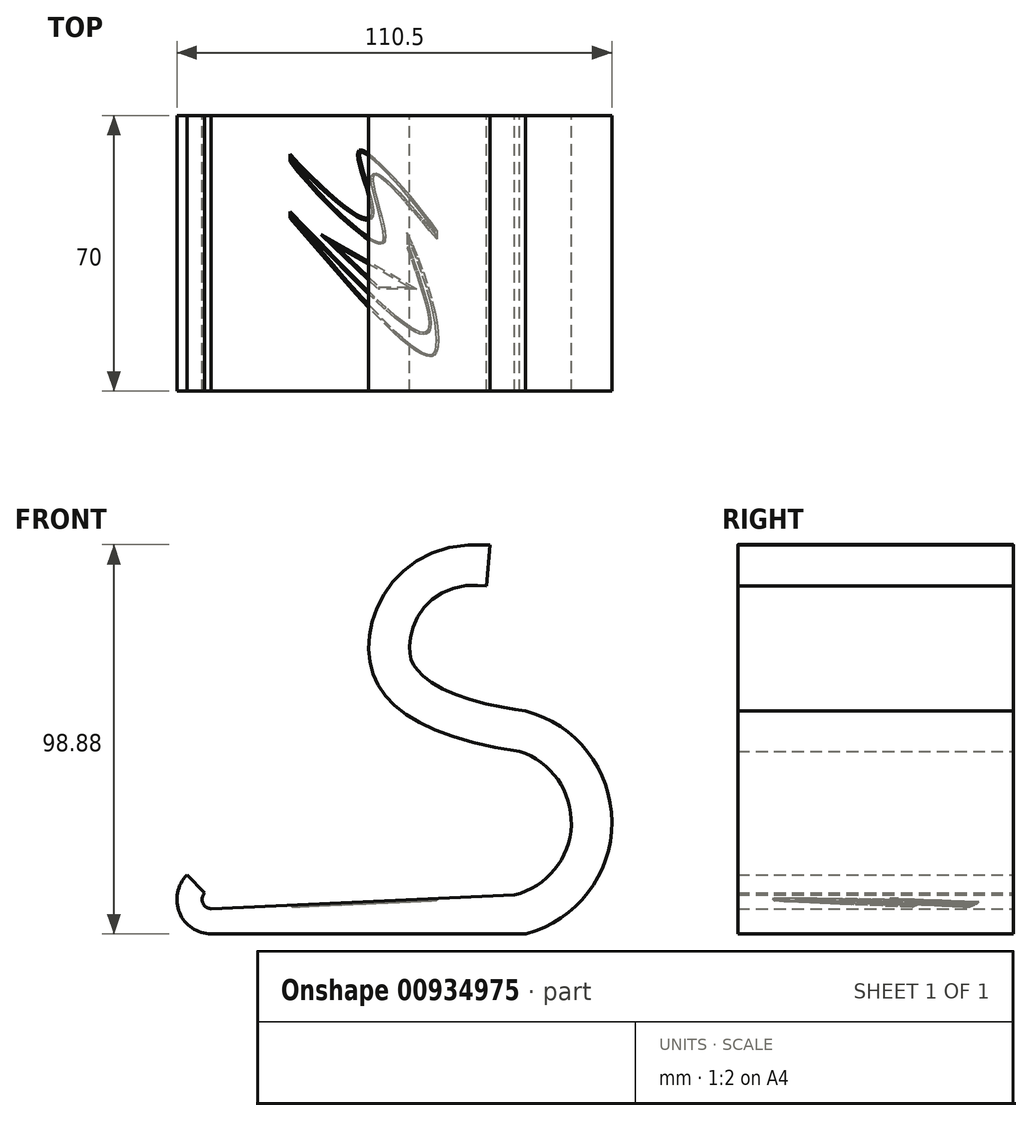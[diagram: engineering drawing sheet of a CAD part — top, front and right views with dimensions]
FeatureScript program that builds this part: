
annotation { "Feature Type Name" : "Feature", "Feature Type Description" : "" }
export const myFeature = defineFeature(function(context is Context, id is Id, definition is map)
    precondition{}
    {
        {
            var Q0;
            Q0=qCreatedBy(makeId("Front.planeOp"),FACE);
            var sketch = newSketch(context, id + "F0", { "sketchPlane" : qUnion([Q0])});
            skLineSegment(sketch, "E0", {"start": v(0, 0) * mm, "end": v(0, 100) * mm, "construction": true});
            skLineSegment(sketch, "E1", {"start": v(0, 0) * mm, "end": v(-40, 0) * mm});
            skLineSegment(sketch, "E2", {"start": v(0, 0) * mm, "end": v(40, 0) * mm});
            skArc(sketch, "E3", {"start": v(-46.17, 14.93) * mm, "mid": v(-48.08, 5.4) * mm, "end": v(-40, 0) * mm});
            skArc(sketch, "E4.2", {"start": v(37.04, 9.88) * mm, "mid": v(51.45, 27.63) * mm, "end": v(38.33, 46.36) * mm});
            skArc(sketch, "E5.0", {"start": v(-41.65, 10.4) * mm, "mid": v(-42.16, 7.85) * mm, "end": v(-40, 6.4) * mm});
            skLineSegment(sketch, "E6", {"start": v(37.04, 9.88) * mm, "end": v(-40, 6.4) * mm});
            skLineSegment(sketch, "E7", {"start": v(-41.65, 10.4) * mm, "end": v(-46.17, 14.93) * mm});
            skFitSpline(sketch, "E8", {"points": [v(38.33, 46.36) * mm, v(0, 71.82) * mm, v(30.83, 98.74) * mm], "startDerivative": vector(-149.61, 21.91) * mm, "endDerivative": vector(132.7, -11.42) * mm});
            skFitSpline(sketch, "E9.0", {"points": [v(39.83, 56.65) * mm, v(36.93, 57.08) * mm, v(31.58, 58.05) * mm, v(24.9, 59.83) * mm, v(19.6, 61.84) * mm, v(15.7, 63.97) * mm, v(13.54, 65.69) * mm, v(12.36, 66.96) * mm, v(11.7, 67.86) * mm, v(11.2, 68.72) * mm, v(10.84, 69.6) * mm, v(10.57, 70.56) * mm, v(10.4, 71.63) * mm, v(10.36, 72.9) * mm, v(10.49, 74.79) * mm, v(11.05, 77.38) * mm, v(12.41, 80.49) * mm, v(14.4, 83.28) * mm, v(16.96, 85.58) * mm, v(20.16, 87.34) * mm, v(24.28, 88.44) * mm, v(27.89, 88.55) * mm, v(29.94, 88.38) * mm]});
            skLineSegment(sketch, "E10", {"start": v(29.94, 88.38) * mm, "end": v(30.83, 98.74) * mm});
            skArc(sketch, "E11.0", {"start": v(40, 0) * mm, "mid": v(61.76, 28.4) * mm, "end": v(39.8, 56.66) * mm});
            skSolve(sketch);
        }
        {
            var Q0;
            Q0=makeQuery(id+"F0.imprint","IMPRINT",FACE,{"disambiguationData":[TD([[makeQuery(id+"F0.imprint","IMPRINT",EDGE,{"derivedFrom":sQuery(id+"F0.wireOp",EDGE,"E1")}),-1.0]])]});
            extrude(context, id + "F1", {"entities" : qUnion([Q0]), "depth" : 35 * mm, "offsetDistance" : 25 * mm, "hasSecondDirection" : true, "secondDirectionOppositeDirection" : true, "secondDirectionDepth" : 35 * mm});
        }
        {
            var Q0;
            Q0=makeQuery(id+"F1.opExtrude","SWEPT_FACE",FACE,{"disambiguationData":[OSD([sQuery(id+"F0.wireOp",EDGE,"E6")])]});
            var sketch = newSketch(context, id + "F2", { "sketchPlane" : qUnion([Q0])});
            skPoint(sketch, "E12.positionSnap0", {"position": v(-39.67, 0) * mm});
            skPoint(sketch, "E12.positionSnap1", {"position": v(-1.11, 35) * mm});
            skLineSegment(sketch, "E13", {"start": v(-19.66, 10.69) * mm, "end": v(-19.66, 8.95) * mm});
            skLineSegment(sketch, "E14", {"start": v(-19.66, 25.24) * mm, "end": v(-19.66, 23.32) * mm});
            skLineSegment(sketch, "E15.MirrorCS", {"start": v(-1.77, 26.28) * mm, "end": v(-2.06, 26.21) * mm});
            skLineSegment(sketch, "E16.MirrorCS", {"start": v(1.54, 19.5) * mm, "end": v(1.46, 19.02) * mm});
            skLineSegment(sketch, "E17.MirrorCS", {"start": v(1.77, 19.78) * mm, "end": v(1.54, 19.5) * mm});
            skLineSegment(sketch, "E18.MirrorCS", {"start": v(1.46, 19.02) * mm, "end": v(1.48, 18.36) * mm});
            skLineSegment(sketch, "E19.MirrorCS", {"start": v(-2.06, 26.21) * mm, "end": v(-2.27, 26.01) * mm});
            skLineSegment(sketch, "E20.MirrorCS", {"start": v(-2.4, 25.63) * mm, "end": v(-2.44, 25.1) * mm});
            skLineSegment(sketch, "E21.MirrorCS", {"start": v(-2.27, 26.01) * mm, "end": v(-2.4, 25.63) * mm});
            skLineSegment(sketch, "E22.MirrorCS", {"start": v(-1.4, 26.23) * mm, "end": v(-1.77, 26.28) * mm});
            skLineSegment(sketch, "E23.MirrorCS", {"start": v(1.07, 10.9) * mm, "end": v(1.08, 10.23) * mm});
            skLineSegment(sketch, "E24.MirrorCS", {"start": v(1.08, 10.23) * mm, "end": v(0.99, 9.69) * mm});
            skLineSegment(sketch, "E25.MirrorCS", {"start": v(-2.45, 9.75) * mm, "end": v(-4.03, 10.74) * mm});
            skLineSegment(sketch, "E26.MirrorCS", {"start": v(12.35, -24.75) * mm, "end": v(10.73, -23.6) * mm});
            skLineSegment(sketch, "E27.MirrorCS", {"start": v(1.96, 24) * mm, "end": v(0.86, 24.9) * mm});
            skLineSegment(sketch, "E28.MirrorCS", {"start": v(4.57, 3.56) * mm, "end": v(4.45, 3.08) * mm});
            skLineSegment(sketch, "E29.MirrorCS", {"start": v(14.83, -20.03) * mm, "end": v(14.33, -20.12) * mm});
            skLineSegment(sketch, "E30.MirrorCS", {"start": v(18.11, -22) * mm, "end": v(18, -23.76) * mm});
            skLineSegment(sketch, "E31.MirrorCS", {"start": v(-0.37, 8.93) * mm, "end": v(-1.32, 9.2) * mm});
            skLineSegment(sketch, "E32.MirrorCS", {"start": v(2.14, 19.84) * mm, "end": v(1.77, 19.78) * mm});
            skLineSegment(sketch, "E33.MirrorCS", {"start": v(15.84, -26.22) * mm, "end": v(15.06, -26.1) * mm});
            skLineSegment(sketch, "E34.MirrorCS", {"start": v(3.46, 2.33) * mm, "end": v(2.81, 2.39) * mm});
            skLineSegment(sketch, "E35.MirrorCS", {"start": v(0.99, 9.69) * mm, "end": v(0.64, 9.12) * mm});
            skLineSegment(sketch, "E36.MirrorCS", {"start": v(15.68, -17.7) * mm, "end": v(15.62, -18.72) * mm});
            skLineSegment(sketch, "E37.MirrorCS", {"start": v(-0.11, 25.6) * mm, "end": v(-0.94, 26.07) * mm});
            skLineSegment(sketch, "E38.MirrorCS", {"start": v(17.05, -25.85) * mm, "end": v(16.5, -26.14) * mm});
            skLineSegment(sketch, "E39.MirrorCS", {"start": v(6.33, 16.67) * mm, "end": v(4.91, 18.02) * mm});
            skLineSegment(sketch, "E40.MirrorCS", {"start": v(4.91, 18.02) * mm, "end": v(3.69, 19.04) * mm});
            skLineSegment(sketch, "E41.MirrorCS", {"start": v(2.03, 15.55) * mm, "end": v(2.46, 13.92) * mm});
            skLineSegment(sketch, "E42.MirrorCS", {"start": v(-1.32, 9.2) * mm, "end": v(-2.45, 9.75) * mm});
            skLineSegment(sketch, "E43.MirrorCS", {"start": v(15.47, -19.32) * mm, "end": v(15.2, -19.76) * mm});
            skLineSegment(sketch, "E44.MirrorCS", {"start": v(14.33, -20.12) * mm, "end": v(13.45, -19.98) * mm});
            skLineSegment(sketch, "E45.MirrorCS", {"start": v(2.82, 19.6) * mm, "end": v(2.14, 19.84) * mm});
            skLineSegment(sketch, "E46.MirrorCS", {"start": v(3.69, 19.04) * mm, "end": v(2.82, 19.6) * mm});
            skLineSegment(sketch, "E47.MirrorCS", {"start": v(11.07, -18.77) * mm, "end": v(9.33, -17.55) * mm});
            skLineSegment(sketch, "E48.MirrorCS", {"start": v(15.2, -19.76) * mm, "end": v(14.83, -20.03) * mm});
            skLineSegment(sketch, "E49.MirrorCS", {"start": v(0.78, 3.26) * mm, "end": v(-0.67, 4.19) * mm});
            skLineSegment(sketch, "E50.MirrorCS", {"start": v(13.45, -19.98) * mm, "end": v(12.36, -19.52) * mm});
            skLineSegment(sketch, "E51.MirrorCS", {"start": v(17.48, -25.35) * mm, "end": v(17.05, -25.85) * mm});
            skLineSegment(sketch, "E52.MirrorCS", {"start": v(0.2, 8.93) * mm, "end": v(-0.37, 8.93) * mm});
            skLineSegment(sketch, "E53.MirrorCS", {"start": v(15.33, -14.96) * mm, "end": v(15.58, -16.43) * mm});
            skLineSegment(sketch, "E54.MirrorCS", {"start": v(0.86, 24.9) * mm, "end": v(-0.11, 25.6) * mm});
            skLineSegment(sketch, "E55.MirrorCS", {"start": v(18, -23.76) * mm, "end": v(17.8, -24.64) * mm});
            skLineSegment(sketch, "E56.MirrorCS", {"start": v(13.8, -25.6) * mm, "end": v(12.35, -24.75) * mm});
            skLineSegment(sketch, "E57.MirrorCS", {"start": v(0.86, 12.4) * mm, "end": v(1.07, 10.9) * mm});
            skLineSegment(sketch, "E58.MirrorCS", {"start": v(2.05, 2.63) * mm, "end": v(0.78, 3.26) * mm});
            skLineSegment(sketch, "E59.MirrorCS", {"start": v(4.45, 3.08) * mm, "end": v(4.25, 2.71) * mm});
            skLineSegment(sketch, "E60.MirrorCS", {"start": v(1.48, 18.36) * mm, "end": v(1.7, 17) * mm});
            skLineSegment(sketch, "E61.MirrorCS", {"start": v(3.96, 2.47) * mm, "end": v(3.46, 2.33) * mm});
            skLineSegment(sketch, "E62.MirrorCS", {"start": v(15.06, -26.1) * mm, "end": v(13.8, -25.6) * mm});
            skLineSegment(sketch, "E63.MirrorCS", {"start": v(4.25, 2.71) * mm, "end": v(3.96, 2.47) * mm});
            skLineSegment(sketch, "E64.MirrorCS", {"start": v(4.62, 4.15) * mm, "end": v(4.57, 3.56) * mm});
            skLineSegment(sketch, "E65.MirrorCS", {"start": v(0.64, 9.12) * mm, "end": v(0.2, 8.93) * mm});
            skLineSegment(sketch, "E66.MirrorCS", {"start": v(4.5, 5.71) * mm, "end": v(4.62, 4.15) * mm});
            skLineSegment(sketch, "E67.MirrorCS", {"start": v(1.7, 17) * mm, "end": v(2.03, 15.55) * mm});
            skLineSegment(sketch, "E68.MirrorCS", {"start": v(15.58, -16.43) * mm, "end": v(15.68, -17.7) * mm});
            skLineSegment(sketch, "E69.MirrorCS", {"start": v(12.36, -19.52) * mm, "end": v(11.07, -18.77) * mm});
            skLineSegment(sketch, "E70.MirrorCS", {"start": v(15.62, -18.72) * mm, "end": v(15.47, -19.32) * mm});
            skLineSegment(sketch, "E71.MirrorCS", {"start": v(-2.44, 25.1) * mm, "end": v(-2.32, 24.01) * mm});
            skLineSegment(sketch, "E72.MirrorCS", {"start": v(2.81, 2.39) * mm, "end": v(2.05, 2.63) * mm});
            skLineSegment(sketch, "E73.MirrorCS", {"start": v(16.5, -26.14) * mm, "end": v(15.84, -26.22) * mm});
            skLineSegment(sketch, "E74.MirrorCS", {"start": v(17.8, -24.64) * mm, "end": v(17.48, -25.35) * mm});
            skLineSegment(sketch, "E75.MirrorCS", {"start": v(-0.94, 26.07) * mm, "end": v(-1.4, 26.23) * mm});
            skLineSegment(sketch, "E76.MirrorCS", {"start": v(-4.01, 6.8) * mm, "end": v(-6.92, 9.42) * mm});
            skLineSegment(sketch, "E77.MirrorCS", {"start": v(6.92, 19.12) * mm, "end": v(5.17, 20.95) * mm});
            skLineSegment(sketch, "E78.MirrorCS", {"start": v(-2.28, 5.38) * mm, "end": v(-4.01, 6.8) * mm});
            skLineSegment(sketch, "E79.MirrorCS", {"start": v(-17.56, 20.72) * mm, "end": v(-19.66, 23.32) * mm});
            skLineSegment(sketch, "E80.MirrorCS", {"start": v(16.5, -12.1) * mm, "end": v(17.17, -14.89) * mm});
            skLineSegment(sketch, "E81.MirrorCS", {"start": v(15.85, 5.86) * mm, "end": v(13.81, 8.3) * mm});
            skLineSegment(sketch, "E82.MirrorCS", {"start": v(-7.7, 13.6) * mm, "end": v(-9.72, 15.35) * mm});
            skLineSegment(sketch, "E83.MirrorCS", {"start": v(12.92, 12.2) * mm, "end": v(10.98, 14.55) * mm});
            skLineSegment(sketch, "E84.MirrorCS", {"start": v(4.75, -13.73) * mm, "end": v(1.89, -11.1) * mm});
            skLineSegment(sketch, "E85.MirrorCS", {"start": v(9.33, -17.55) * mm, "end": v(7.36, -15.98) * mm});
            skLineSegment(sketch, "E86.MirrorCS", {"start": v(3.63, 9.66) * mm, "end": v(4.14, 7.59) * mm});
            skLineSegment(sketch, "E87.MirrorCS", {"start": v(4.14, 7.59) * mm, "end": v(4.5, 5.71) * mm});
            skLineSegment(sketch, "E88.MirrorCS", {"start": v(8.62, -21.86) * mm, "end": v(6.34, -19.78) * mm});
            skLineSegment(sketch, "E89.MirrorCS", {"start": v(-9.78, -2.45) * mm, "end": v(-13.21, 1.5) * mm});
            skLineSegment(sketch, "E90.MirrorCS", {"start": v(-0.12, 16.19) * mm, "end": v(0.46, 14.14) * mm});
            skLineSegment(sketch, "E91.MirrorCS", {"start": v(7.87, 15.07) * mm, "end": v(6.33, 16.67) * mm});
            skLineSegment(sketch, "E92.MirrorCS", {"start": v(11.67, 10.82) * mm, "end": v(9.52, 13.27) * mm});
            skLineSegment(sketch, "E93.MirrorCS", {"start": v(-15.17, 17.96) * mm, "end": v(-17.56, 20.72) * mm});
            skLineSegment(sketch, "E94.MirrorCS", {"start": v(0.36, -13.74) * mm, "end": v(-2.82, -10.3) * mm});
            skLineSegment(sketch, "E95.MirrorCS", {"start": v(2.46, 13.92) * mm, "end": v(3.05, 11.8) * mm});
            skLineSegment(sketch, "E96.MirrorCS", {"start": v(7.36, -15.98) * mm, "end": v(4.75, -13.73) * mm});
            skLineSegment(sketch, "E97.MirrorCS", {"start": v(-4.03, 10.74) * mm, "end": v(-5.8, 12.04) * mm});
            skLineSegment(sketch, "E98.MirrorCS", {"start": v(3.05, 11.8) * mm, "end": v(3.63, 9.66) * mm});
            skLineSegment(sketch, "E99.MirrorCS", {"start": v(-1.95, 22.34) * mm, "end": v(-1.4, 20.4) * mm});
            skLineSegment(sketch, "E100.MirrorCS", {"start": v(12.47, -9) * mm, "end": v(2.77, -9) * mm});
            skLineSegment(sketch, "E101.MirrorCS", {"start": v(-6.92, 9.42) * mm, "end": v(-9.92, 12.35) * mm});
            skLineSegment(sketch, "E102.MirrorCS", {"start": v(8.96, 16.88) * mm, "end": v(6.92, 19.12) * mm});
            skLineSegment(sketch, "E103.MirrorCS", {"start": v(11.53, 2.25) * mm, "end": v(12.92, -1.11) * mm});
            skLineSegment(sketch, "E104.MirrorCS", {"start": v(15.46, -8.42) * mm, "end": v(16.5, -12.1) * mm});
            skLineSegment(sketch, "E105.MirrorCS", {"start": v(16.34, 7.78) * mm, "end": v(14.73, 9.92) * mm});
            skLineSegment(sketch, "E106.MirrorCS", {"start": v(14.25, -4.71) * mm, "end": v(15.46, -8.42) * mm});
            skLineSegment(sketch, "E107.MirrorCS", {"start": v(6.34, -19.78) * mm, "end": v(3.43, -16.93) * mm});
            skLineSegment(sketch, "E108.MirrorCS", {"start": v(13.22, -7.42) * mm, "end": v(14.09, -10.17) * mm});
            skLineSegment(sketch, "E109.MirrorCS", {"start": v(10.11, 5.24) * mm, "end": v(11.53, 2.25) * mm});
            skLineSegment(sketch, "E110.MirrorCS", {"start": v(-4.67, -4.7) * mm, "end": v(-8.3, -1.02) * mm});
            skLineSegment(sketch, "E111.MirrorCS", {"start": v(-15.85, 6.74) * mm, "end": v(-19.66, 10.69) * mm});
            skLineSegment(sketch, "E112.MirrorCS", {"start": v(1.89, -11.1) * mm, "end": v(-1.19, -8.14) * mm});
            skLineSegment(sketch, "E113.MirrorCS", {"start": v(9.52, 13.27) * mm, "end": v(7.87, 15.07) * mm});
            skLineSegment(sketch, "E114.MirrorCS", {"start": v(14.09, -10.17) * mm, "end": v(14.8, -12.7) * mm});
            skLineSegment(sketch, "E115.MirrorCS", {"start": v(10.98, 14.55) * mm, "end": v(8.96, 16.88) * mm});
            skLineSegment(sketch, "E116.MirrorCS", {"start": v(-11.76, 4.77) * mm, "end": v(2.77, -9) * mm});
            skLineSegment(sketch, "E117.MirrorCS", {"start": v(13.81, 8.3) * mm, "end": v(11.67, 10.82) * mm});
            skLineSegment(sketch, "E118.MirrorCS", {"start": v(-1.4, 20.4) * mm, "end": v(-0.77, 18.32) * mm});
            skLineSegment(sketch, "E119.MirrorCS", {"start": v(10.11, 1.53) * mm, "end": v(11.2, -1.51) * mm});
            skLineSegment(sketch, "E120.MirrorCS", {"start": v(10.11, 5.24) * mm, "end": v(10.11, 1.53) * mm});
            skLineSegment(sketch, "E121.MirrorCS", {"start": v(-12.05, 2.82) * mm, "end": v(-15.85, 6.74) * mm});
            skLineSegment(sketch, "E122.MirrorCS", {"start": v(17.69, 5.87) * mm, "end": v(16.34, 7.78) * mm});
            skLineSegment(sketch, "E123.MirrorCS", {"start": v(17.67, -17.51) * mm, "end": v(18, -19.9) * mm});
            skLineSegment(sketch, "E124.MirrorCS", {"start": v(3.5, 22.6) * mm, "end": v(1.96, 24) * mm});
            skLineSegment(sketch, "E125.MirrorCS", {"start": v(-5.8, 12.04) * mm, "end": v(-7.7, 13.6) * mm});
            skLineSegment(sketch, "E126.MirrorCS", {"start": v(12.47, -9) * mm, "end": v(-11.76, 4.77) * mm});
            skLineSegment(sketch, "E127.MirrorCS", {"start": v(14.73, 9.92) * mm, "end": v(12.92, 12.2) * mm});
            skLineSegment(sketch, "E128.MirrorCS", {"start": v(5.17, 20.95) * mm, "end": v(3.5, 22.6) * mm});
            skLineSegment(sketch, "E129.MirrorCS", {"start": v(10.73, -23.6) * mm, "end": v(8.62, -21.86) * mm});
            skLineSegment(sketch, "E130.MirrorCS", {"start": v(-17.18, 22.6) * mm, "end": v(-19.66, 25.24) * mm});
            skLineSegment(sketch, "E131.MirrorCS", {"start": v(-0.77, 18.32) * mm, "end": v(-0.12, 16.19) * mm});
            skLineSegment(sketch, "E132.MirrorCS", {"start": v(17.69, 3.63) * mm, "end": v(15.85, 5.86) * mm});
            skLineSegment(sketch, "E133.MirrorCS", {"start": v(0.46, 14.14) * mm, "end": v(0.86, 12.4) * mm});
            skLineSegment(sketch, "E134.MirrorCS", {"start": v(18, -19.9) * mm, "end": v(18.11, -22) * mm});
            skLineSegment(sketch, "E135.MirrorCS", {"start": v(3.43, -16.93) * mm, "end": v(0.36, -13.74) * mm});
            skLineSegment(sketch, "E136.MirrorCS", {"start": v(12.92, -1.11) * mm, "end": v(14.25, -4.71) * mm});
            skLineSegment(sketch, "E137.MirrorCS", {"start": v(-8.3, -1.02) * mm, "end": v(-12.05, 2.82) * mm});
            skLineSegment(sketch, "E138.MirrorCS", {"start": v(-9.92, 12.35) * mm, "end": v(-12.6, 15.14) * mm});
            skLineSegment(sketch, "E139.MirrorCS", {"start": v(-0.67, 4.19) * mm, "end": v(-2.28, 5.38) * mm});
            skLineSegment(sketch, "E140.MirrorCS", {"start": v(-9.72, 15.35) * mm, "end": v(-11.8, 17.26) * mm});
            skLineSegment(sketch, "E141.MirrorCS", {"start": v(-16.53, 5.34) * mm, "end": v(-19.66, 8.95) * mm});
            skLineSegment(sketch, "E142.MirrorCS", {"start": v(-12.6, 15.14) * mm, "end": v(-15.17, 17.96) * mm});
            skLineSegment(sketch, "E143.MirrorCS", {"start": v(-6.3, -6.42) * mm, "end": v(-9.78, -2.45) * mm});
            skLineSegment(sketch, "E144.MirrorCS", {"start": v(17.17, -14.89) * mm, "end": v(17.67, -17.51) * mm});
            skLineSegment(sketch, "E145.MirrorCS", {"start": v(12.24, -4.52) * mm, "end": v(13.22, -7.42) * mm});
            skLineSegment(sketch, "E146.MirrorCS", {"start": v(17.69, 5.87) * mm, "end": v(17.69, 3.63) * mm});
            skLineSegment(sketch, "E147.MirrorCS", {"start": v(-2.32, 24.01) * mm, "end": v(-1.95, 22.34) * mm});
            skLineSegment(sketch, "E148.MirrorCS", {"start": v(11.2, -1.51) * mm, "end": v(12.24, -4.52) * mm});
            skLineSegment(sketch, "E149.MirrorCS", {"start": v(14.8, -12.7) * mm, "end": v(15.33, -14.96) * mm});
            skLineSegment(sketch, "E150.MirrorCS", {"start": v(-14.53, 19.9) * mm, "end": v(-17.18, 22.6) * mm});
            skLineSegment(sketch, "E151.MirrorCS", {"start": v(-13.21, 1.5) * mm, "end": v(-16.53, 5.34) * mm});
            skLineSegment(sketch, "E152.MirrorCS", {"start": v(-1.19, -8.14) * mm, "end": v(-4.67, -4.7) * mm});
            skLineSegment(sketch, "E153.MirrorCS", {"start": v(-11.8, 17.26) * mm, "end": v(-14.53, 19.9) * mm});
            skLineSegment(sketch, "E154.MirrorCS", {"start": v(-2.82, -10.3) * mm, "end": v(-6.3, -6.42) * mm});
            skPoint(sketch, "E155.endSnap0", {"position": v(-17.76, 8.71) * mm});
            skSolve(sketch);
        }
        {
            var Q0;
            Q0=makeQuery(id+"F2.imprint","IMPRINT",FACE,{"disambiguationData":[TD([[makeQuery(id+"F2.imprint","IMPRINT",EDGE,{"derivedFrom":sQuery(id+"F2.wireOp",EDGE,"E15.MirrorCS")}),1.0]])]});
            var Q1;
            Q1=makeQuery(id+"F2.imprint","IMPRINT",FACE,{"disambiguationData":[TD([[makeQuery(id+"F2.imprint","IMPRINT",EDGE,{"derivedFrom":sQuery(id+"F2.wireOp",EDGE,"E100.MirrorCS")}),-1.0]])]});
            var Q2;
            Q2=makeQuery(id+"F2.imprint","IMPRINT",FACE,{"disambiguationData":[TD([[makeQuery(id+"F2.imprint","IMPRINT",EDGE,{"derivedFrom":sQuery(id+"F2.wireOp",EDGE,"E13")}),1.0]])]});
            extrude(context, id + "F3", {"entities" : qUnion([Q0, Q1, Q2]), "operationType" : NewBodyOperationType.REMOVE, "oppositeDirection" : true, "depth" : 0.5 * mm, "offsetDistance" : 25 * mm});
        }
        {
            var Q0;
            Q0=makeQuery(id+"F3.boolean.opBoolean","COPY",FACE,{"derivedFrom":makeQuery(id+"F3.opExtrude","CAP_FACE",FACE,{"disambiguationData":[OSD([sQuery(id+"F2.wireOp",EDGE,"E15.MirrorCS"),sQuery(id+"F2.wireOp",EDGE,"E16.MirrorCS"),sQuery(id+"F2.wireOp",EDGE,"E17.MirrorCS"),sQuery(id+"F2.wireOp",EDGE,"E18.MirrorCS"),sQuery(id+"F2.wireOp",EDGE,"E19.MirrorCS"),sQuery(id+"F2.wireOp",EDGE,"E20.MirrorCS"),sQuery(id+"F2.wireOp",EDGE,"E21.MirrorCS"),sQuery(id+"F2.wireOp",EDGE,"E22.MirrorCS"),sQuery(id+"F2.wireOp",EDGE,"E23.MirrorCS"),sQuery(id+"F2.wireOp",EDGE,"E24.MirrorCS"),sQuery(id+"F2.wireOp",EDGE,"E25.MirrorCS"),sQuery(id+"F2.wireOp",EDGE,"E27.MirrorCS"),sQuery(id+"F2.wireOp",EDGE,"E28.MirrorCS"),sQuery(id+"F2.wireOp",EDGE,"E31.MirrorCS"),sQuery(id+"F2.wireOp",EDGE,"E32.MirrorCS"),sQuery(id+"F2.wireOp",EDGE,"E34.MirrorCS"),sQuery(id+"F2.wireOp",EDGE,"E35.MirrorCS"),sQuery(id+"F2.wireOp",EDGE,"E37.MirrorCS"),sQuery(id+"F2.wireOp",EDGE,"E39.MirrorCS"),sQuery(id+"F2.wireOp",EDGE,"E40.MirrorCS"),sQuery(id+"F2.wireOp",EDGE,"E41.MirrorCS"),sQuery(id+"F2.wireOp",EDGE,"E42.MirrorCS"),sQuery(id+"F2.wireOp",EDGE,"E45.MirrorCS"),sQuery(id+"F2.wireOp",EDGE,"E46.MirrorCS"),sQuery(id+"F2.wireOp",EDGE,"E49.MirrorCS"),sQuery(id+"F2.wireOp",EDGE,"E52.MirrorCS"),sQuery(id+"F2.wireOp",EDGE,"E54.MirrorCS"),sQuery(id+"F2.wireOp",EDGE,"E57.MirrorCS"),sQuery(id+"F2.wireOp",EDGE,"E58.MirrorCS"),sQuery(id+"F2.wireOp",EDGE,"E59.MirrorCS"),sQuery(id+"F2.wireOp",EDGE,"E60.MirrorCS"),sQuery(id+"F2.wireOp",EDGE,"E61.MirrorCS"),sQuery(id+"F2.wireOp",EDGE,"E63.MirrorCS"),sQuery(id+"F2.wireOp",EDGE,"E64.MirrorCS"),sQuery(id+"F2.wireOp",EDGE,"E65.MirrorCS"),sQuery(id+"F2.wireOp",EDGE,"E66.MirrorCS"),sQuery(id+"F2.wireOp",EDGE,"E67.MirrorCS"),sQuery(id+"F2.wireOp",EDGE,"E71.MirrorCS"),sQuery(id+"F2.wireOp",EDGE,"E72.MirrorCS"),sQuery(id+"F2.wireOp",EDGE,"E75.MirrorCS"),sQuery(id+"F2.wireOp",EDGE,"E76.MirrorCS"),sQuery(id+"F2.wireOp",EDGE,"E77.MirrorCS"),sQuery(id+"F2.wireOp",EDGE,"E78.MirrorCS"),sQuery(id+"F2.wireOp",EDGE,"E79.MirrorCS"),sQuery(id+"F2.wireOp",EDGE,"E14"),sQuery(id+"F2.wireOp",EDGE,"E81.MirrorCS"),sQuery(id+"F2.wireOp",EDGE,"E82.MirrorCS"),sQuery(id+"F2.wireOp",EDGE,"E83.MirrorCS"),sQuery(id+"F2.wireOp",EDGE,"E86.MirrorCS"),sQuery(id+"F2.wireOp",EDGE,"E87.MirrorCS"),sQuery(id+"F2.wireOp",EDGE,"E90.MirrorCS"),sQuery(id+"F2.wireOp",EDGE,"E91.MirrorCS"),sQuery(id+"F2.wireOp",EDGE,"E92.MirrorCS"),sQuery(id+"F2.wireOp",EDGE,"E93.MirrorCS"),sQuery(id+"F2.wireOp",EDGE,"E95.MirrorCS"),sQuery(id+"F2.wireOp",EDGE,"E97.MirrorCS"),sQuery(id+"F2.wireOp",EDGE,"E98.MirrorCS"),sQuery(id+"F2.wireOp",EDGE,"E99.MirrorCS"),sQuery(id+"F2.wireOp",EDGE,"E101.MirrorCS"),sQuery(id+"F2.wireOp",EDGE,"E102.MirrorCS"),sQuery(id+"F2.wireOp",EDGE,"E105.MirrorCS"),sQuery(id+"F2.wireOp",EDGE,"E113.MirrorCS"),sQuery(id+"F2.wireOp",EDGE,"E115.MirrorCS"),sQuery(id+"F2.wireOp",EDGE,"E117.MirrorCS"),sQuery(id+"F2.wireOp",EDGE,"E118.MirrorCS"),sQuery(id+"F2.wireOp",EDGE,"E122.MirrorCS"),sQuery(id+"F2.wireOp",EDGE,"E124.MirrorCS"),sQuery(id+"F2.wireOp",EDGE,"E125.MirrorCS"),sQuery(id+"F2.wireOp",EDGE,"E127.MirrorCS"),sQuery(id+"F2.wireOp",EDGE,"E128.MirrorCS"),sQuery(id+"F2.wireOp",EDGE,"E130.MirrorCS"),sQuery(id+"F2.wireOp",EDGE,"E131.MirrorCS"),sQuery(id+"F2.wireOp",EDGE,"E132.MirrorCS"),sQuery(id+"F2.wireOp",EDGE,"E133.MirrorCS"),sQuery(id+"F2.wireOp",EDGE,"E138.MirrorCS"),sQuery(id+"F2.wireOp",EDGE,"E139.MirrorCS"),sQuery(id+"F2.wireOp",EDGE,"E140.MirrorCS"),sQuery(id+"F2.wireOp",EDGE,"E142.MirrorCS"),sQuery(id+"F2.wireOp",EDGE,"E146.MirrorCS"),sQuery(id+"F2.wireOp",EDGE,"E147.MirrorCS"),sQuery(id+"F2.wireOp",EDGE,"E150.MirrorCS"),sQuery(id+"F2.wireOp",EDGE,"E153.MirrorCS")])],"isStart":false})});
            var Q1;
            Q1=makeQuery(id+"F3.boolean.opBoolean","COPY",FACE,{"derivedFrom":makeQuery(id+"F3.opExtrude","CAP_FACE",FACE,{"disambiguationData":[OSD([sQuery(id+"F2.wireOp",EDGE,"E100.MirrorCS"),sQuery(id+"F2.wireOp",EDGE,"E116.MirrorCS"),sQuery(id+"F2.wireOp",EDGE,"E126.MirrorCS")])],"isStart":false})});
            var Q2;
            Q2=makeQuery(id+"F3.boolean.opBoolean","COPY",FACE,{"derivedFrom":makeQuery(id+"F3.opExtrude","CAP_FACE",FACE,{"disambiguationData":[OSD([sQuery(id+"F2.wireOp",EDGE,"E13"),sQuery(id+"F2.wireOp",EDGE,"E26.MirrorCS"),sQuery(id+"F2.wireOp",EDGE,"E29.MirrorCS"),sQuery(id+"F2.wireOp",EDGE,"E30.MirrorCS"),sQuery(id+"F2.wireOp",EDGE,"E33.MirrorCS"),sQuery(id+"F2.wireOp",EDGE,"E36.MirrorCS"),sQuery(id+"F2.wireOp",EDGE,"E38.MirrorCS"),sQuery(id+"F2.wireOp",EDGE,"E43.MirrorCS"),sQuery(id+"F2.wireOp",EDGE,"E44.MirrorCS"),sQuery(id+"F2.wireOp",EDGE,"E47.MirrorCS"),sQuery(id+"F2.wireOp",EDGE,"E48.MirrorCS"),sQuery(id+"F2.wireOp",EDGE,"E50.MirrorCS"),sQuery(id+"F2.wireOp",EDGE,"E51.MirrorCS"),sQuery(id+"F2.wireOp",EDGE,"E53.MirrorCS"),sQuery(id+"F2.wireOp",EDGE,"E55.MirrorCS"),sQuery(id+"F2.wireOp",EDGE,"E56.MirrorCS"),sQuery(id+"F2.wireOp",EDGE,"E62.MirrorCS"),sQuery(id+"F2.wireOp",EDGE,"E68.MirrorCS"),sQuery(id+"F2.wireOp",EDGE,"E69.MirrorCS"),sQuery(id+"F2.wireOp",EDGE,"E70.MirrorCS"),sQuery(id+"F2.wireOp",EDGE,"E73.MirrorCS"),sQuery(id+"F2.wireOp",EDGE,"E74.MirrorCS"),sQuery(id+"F2.wireOp",EDGE,"E80.MirrorCS"),sQuery(id+"F2.wireOp",EDGE,"E84.MirrorCS"),sQuery(id+"F2.wireOp",EDGE,"E85.MirrorCS"),sQuery(id+"F2.wireOp",EDGE,"E88.MirrorCS"),sQuery(id+"F2.wireOp",EDGE,"E89.MirrorCS"),sQuery(id+"F2.wireOp",EDGE,"E94.MirrorCS"),sQuery(id+"F2.wireOp",EDGE,"E96.MirrorCS"),sQuery(id+"F2.wireOp",EDGE,"E103.MirrorCS"),sQuery(id+"F2.wireOp",EDGE,"E104.MirrorCS"),sQuery(id+"F2.wireOp",EDGE,"E106.MirrorCS"),sQuery(id+"F2.wireOp",EDGE,"E107.MirrorCS"),sQuery(id+"F2.wireOp",EDGE,"E108.MirrorCS"),sQuery(id+"F2.wireOp",EDGE,"E109.MirrorCS"),sQuery(id+"F2.wireOp",EDGE,"E110.MirrorCS"),sQuery(id+"F2.wireOp",EDGE,"E111.MirrorCS"),sQuery(id+"F2.wireOp",EDGE,"E112.MirrorCS"),sQuery(id+"F2.wireOp",EDGE,"E114.MirrorCS"),sQuery(id+"F2.wireOp",EDGE,"E119.MirrorCS"),sQuery(id+"F2.wireOp",EDGE,"E120.MirrorCS"),sQuery(id+"F2.wireOp",EDGE,"E121.MirrorCS"),sQuery(id+"F2.wireOp",EDGE,"E123.MirrorCS"),sQuery(id+"F2.wireOp",EDGE,"E129.MirrorCS"),sQuery(id+"F2.wireOp",EDGE,"E134.MirrorCS"),sQuery(id+"F2.wireOp",EDGE,"E135.MirrorCS"),sQuery(id+"F2.wireOp",EDGE,"E136.MirrorCS"),sQuery(id+"F2.wireOp",EDGE,"E137.MirrorCS"),sQuery(id+"F2.wireOp",EDGE,"E141.MirrorCS"),sQuery(id+"F2.wireOp",EDGE,"E143.MirrorCS"),sQuery(id+"F2.wireOp",EDGE,"E144.MirrorCS"),sQuery(id+"F2.wireOp",EDGE,"E145.MirrorCS"),sQuery(id+"F2.wireOp",EDGE,"E148.MirrorCS"),sQuery(id+"F2.wireOp",EDGE,"E149.MirrorCS"),sQuery(id+"F2.wireOp",EDGE,"E151.MirrorCS"),sQuery(id+"F2.wireOp",EDGE,"E152.MirrorCS"),sQuery(id+"F2.wireOp",EDGE,"E154.MirrorCS")])],"isStart":false})});
            chamfer(context, id + "F4", {"entities" : qUnion([Q0, Q1, Q2]), "width" : .5 * mm, "tangentPropagation" : true});
        }
    });
